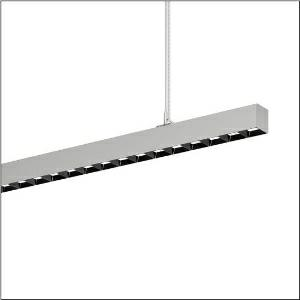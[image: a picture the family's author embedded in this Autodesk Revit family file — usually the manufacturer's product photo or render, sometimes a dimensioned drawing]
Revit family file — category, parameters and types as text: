
# Revit family: silica_r__21_51mx34dc3dsb_1a3f
name_source: partatom
category: Lighting Fixtures
units: mm (PartAtom-declared; Revit-internal decimal feet)

## family parameters
Cut with Voids When Loaded = No
Host = Face
Light Source = No
Part Type = Normal
Room Calculation Point = No
Round Connector Dimension = Use Diameter
Shared = No

## types (1)
- --- (1 x LED, 19200 lm, 129.1 W, 3000K)
    Apparent Load = 129 VA
    CIE Flux Codes = 74 94 99 56 100
    Color Rendering = 80
    Color Temperature = 3000K
    Default Elevation = 1800 mm
    Description = Silica® 21, office luminaire, primary light control with darklight reflector, of PMMA, black, light emission: direct/indirect distribution, primary light characteristic: asymmetric, installation type: suspended mounting, LED, rated luminous flux: 19.200lm, luminous efficacy: 149lm/W, light colour: 830, colour temperature: 3000K, with terminal, 3+2-pole, max. 2.5mm², mains connection: 220..240V, AC, 50/60Hz, rated input power: 129.1W, luminaire housing, of aluminium, metallic grey (RAL 9006), length: 3.004mm, width: 53mm, height: 53mm, protection rating (complete): IP20, insulation class (complete): insulation class I (protective earthing), certification: CE, permissible operating ambient temperature: 0..+35°C, standard: EN 50419, packaging unit: 1 piece
    Height = 53 mm
    Lamp = 1 x LED
    Lamp Light Flux = 19200 lm
    Lamp Power = 129.1 W
    Lamp count = 1
    Length = 3004 mm
    Luminous efficacy = 149 lm/W
    Manufacturer = Siteco
    ModVariant = No
    Model = 51MX34DC3DSB
    Mounting Place = Ceiling
    Mounting Type = Pendant
    Number of Poles = 1
    OnlyDefault = Yes
    Power Factor = 1
    Product Name = Silica® 21
    Product group = office luminaire | ceiling pendant
    ProductGroupID = 905
    Protection Class = Protection class I
    Protection Degree = IP 20
    RLX_Detail_Level = 1
    RlxData = <blob elided: 66697 chars, md5=febee004>
    Socket = socket
    Standby Power = 0 W
    System Light Flux = 19200 lm
    System Power = 129 W
    Type Comments = factory setting: luminous flux: 100 % | dim-lin: 254 | 448 mA
    Type Image = l_1251731.jpg
    URL = http://relux.com
    VarID = @adj_028901
    Voltage = 0 V
    Weight = 0.00 kg
    Width = 53 mm

## geometry (parser evidence)
native form markers: Blend x4, Sweep x12
no freeform markers — native parametric forms only
